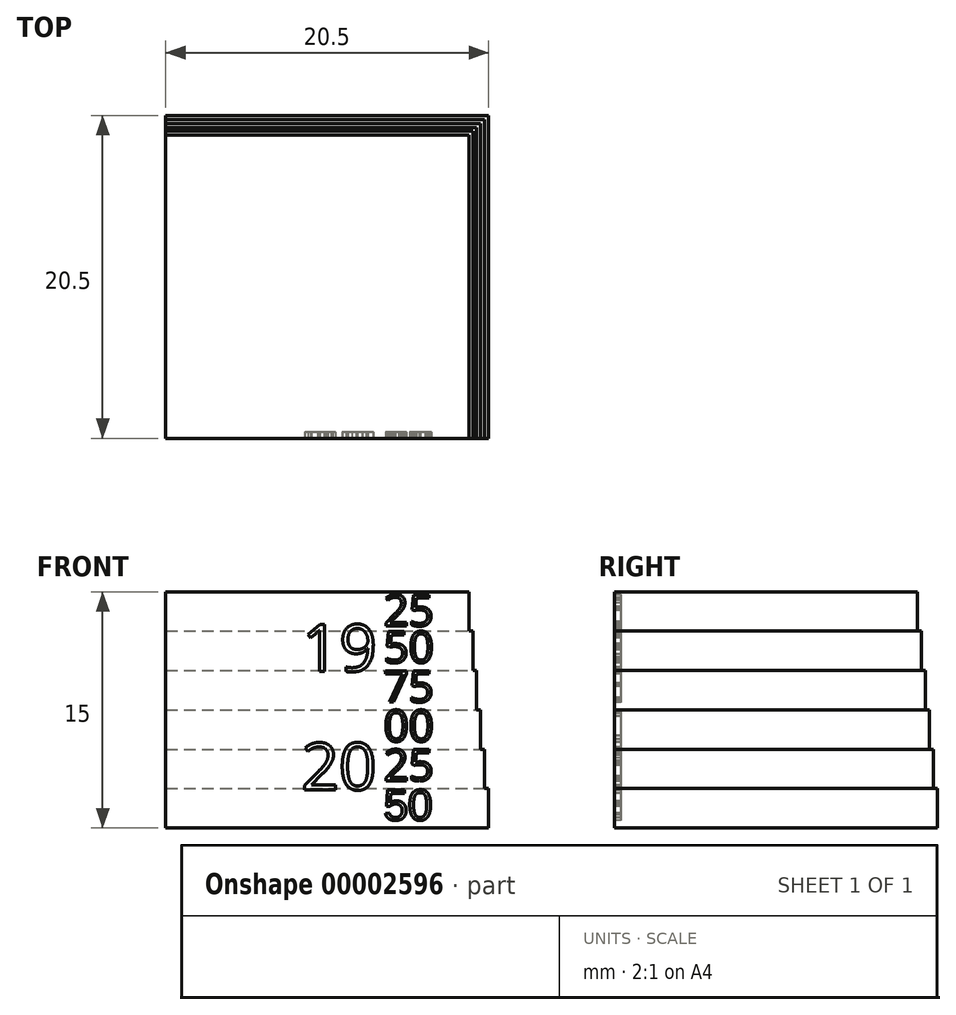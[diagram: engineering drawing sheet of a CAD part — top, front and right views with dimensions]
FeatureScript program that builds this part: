
annotation { "Feature Type Name" : "Feature", "Feature Type Description" : "" }
export const myFeature = defineFeature(function(context is Context, id is Id, definition is map)
    precondition{}
    {
        {
            var Q0;
            Q0=qCreatedBy(makeId("Top.planeOp"),FACE);
            var sketch = newSketch(context, id + "F0", { "sketchPlane" : qUnion([Q0])});
            skLineSegment(sketch, "E0.bottom", {"start": v(0, 0) * mm, "end": v(20.5, 0) * mm});
            skLineSegment(sketch, "E0.top", {"start": v(0, 20.5) * mm, "end": v(20.5, 20.5) * mm});
            skLineSegment(sketch, "E0.left", {"start": v(0, 0) * mm, "end": v(0, 20.5) * mm});
            skLineSegment(sketch, "E0.right", {"start": v(20.5, 0) * mm, "end": v(20.5, 20.5) * mm});
            skSolve(sketch);
        }
        {
            var Q0;
            Q0=makeQuery(id+"F0.imprint","IMPRINT",FACE,{"disambiguationData":[TD([[makeQuery(id+"F0.imprint","IMPRINT",EDGE,{"derivedFrom":sQuery(id+"F0.wireOp",EDGE,"E0.bottom")}),1.0]])]});
            extrude(context, id + "F1", {"entities" : qUnion([Q0]), "depth" : 2.5 * mm});
        }
        {
            var Q0;
            Q0=makeQuery(id+"F1.opExtrude","CAP_FACE",FACE,{"disambiguationData":[OSD([sQuery(id+"F0.wireOp",EDGE,"E0.bottom"),sQuery(id+"F0.wireOp",EDGE,"E0.top"),sQuery(id+"F0.wireOp",EDGE,"E0.left"),sQuery(id+"F0.wireOp",EDGE,"E0.right")])],"isStart":false});
            var sketch = newSketch(context, id + "F2", { "sketchPlane" : qUnion([Q0])});
            skLineSegment(sketch, "E1.bottom", {"start": v(0, 0) * mm, "end": v(20.25, 0) * mm});
            skLineSegment(sketch, "E1.top", {"start": v(0, 20.25) * mm, "end": v(20.25, 20.25) * mm});
            skLineSegment(sketch, "E1.left", {"start": v(0, 0) * mm, "end": v(0, 20.25) * mm});
            skLineSegment(sketch, "E1.right", {"start": v(20.25, 0) * mm, "end": v(20.25, 20.25) * mm});
            skSolve(sketch);
        }
        {
            var Q0;
            Q0 = qSketchRegion(id + "F2", true);
            extrude(context, id + "F3", {"entities" : qUnion([Q0]), "operationType" : NewBodyOperationType.ADD, "depth" : 2.5 * mm});
        }
        {
            var Q0;
            Q0=makeQuery(id+"F3.opExtrude","CAP_FACE",FACE,{"disambiguationData":[OSD([sQuery(id+"F2.wireOp",EDGE,"E1.bottom"),sQuery(id+"F2.wireOp",EDGE,"E1.top"),sQuery(id+"F2.wireOp",EDGE,"E1.left"),sQuery(id+"F2.wireOp",EDGE,"E1.right")])],"isStart":false});
            var sketch = newSketch(context, id + "F4", { "sketchPlane" : qUnion([Q0])});
            skLineSegment(sketch, "E2.bottom", {"start": v(0, 0) * mm, "end": v(20, 0) * mm});
            skLineSegment(sketch, "E2.top", {"start": v(0, 20) * mm, "end": v(20, 20) * mm});
            skLineSegment(sketch, "E2.left", {"start": v(0, 0) * mm, "end": v(0, 20) * mm});
            skLineSegment(sketch, "E2.right", {"start": v(20, 0) * mm, "end": v(20, 20) * mm});
            skSolve(sketch);
        }
        {
            var Q0;
            Q0 = qSketchRegion(id + "F4", true);
            extrude(context, id + "F5", {"entities" : qUnion([Q0]), "operationType" : NewBodyOperationType.ADD, "depth" : 2.5 * mm});
        }
        {
            var Q0;
            Q0=makeQuery(id+"F5.opExtrude","CAP_FACE",FACE,{"disambiguationData":[OSD([sQuery(id+"F4.wireOp",EDGE,"E2.bottom"),sQuery(id+"F4.wireOp",EDGE,"E2.top"),sQuery(id+"F4.wireOp",EDGE,"E2.left"),sQuery(id+"F4.wireOp",EDGE,"E2.right")])],"isStart":false});
            var sketch = newSketch(context, id + "F6", { "sketchPlane" : qUnion([Q0])});
            skLineSegment(sketch, "E3.bottom", {"start": v(0, 0) * mm, "end": v(19.75, 0) * mm});
            skLineSegment(sketch, "E3.top", {"start": v(0, 19.75) * mm, "end": v(19.75, 19.75) * mm});
            skLineSegment(sketch, "E3.left", {"start": v(0, 0) * mm, "end": v(0, 19.75) * mm});
            skLineSegment(sketch, "E3.right", {"start": v(19.75, 0) * mm, "end": v(19.75, 19.75) * mm});
            skSolve(sketch);
        }
        {
            var Q0;
            Q0=makeQuery(id+"F6.imprint","IMPRINT",FACE,{"disambiguationData":[TD([[makeQuery(id+"F6.imprint","IMPRINT",EDGE,{"derivedFrom":sQuery(id+"F6.wireOp",EDGE,"E3.bottom")}),1.0]])]});
            extrude(context, id + "F7", {"entities" : qUnion([Q0]), "operationType" : NewBodyOperationType.ADD, "depth" : 2.5 * mm});
        }
        {
            var Q0;
            Q0=makeQuery(id+"F7.opExtrude","CAP_FACE",FACE,{"disambiguationData":[OSD([sQuery(id+"F6.wireOp",EDGE,"E3.bottom"),sQuery(id+"F6.wireOp",EDGE,"E3.top"),sQuery(id+"F6.wireOp",EDGE,"E3.left"),sQuery(id+"F6.wireOp",EDGE,"E3.right")])],"isStart":false});
            var sketch = newSketch(context, id + "F8", { "sketchPlane" : qUnion([Q0])});
            skLineSegment(sketch, "E4.bottom", {"start": v(0, 0) * mm, "end": v(19.5, 0) * mm});
            skLineSegment(sketch, "E4.top", {"start": v(0, 19.5) * mm, "end": v(19.5, 19.5) * mm});
            skLineSegment(sketch, "E4.left", {"start": v(0, 0) * mm, "end": v(0, 19.5) * mm});
            skLineSegment(sketch, "E4.right", {"start": v(19.5, 0) * mm, "end": v(19.5, 19.5) * mm});
            skSolve(sketch);
        }
        {
            var Q0;
            Q0 = qSketchRegion(id + "F8", true);
            extrude(context, id + "F9", {"entities" : qUnion([Q0]), "operationType" : NewBodyOperationType.ADD, "depth" : 2.5 * mm});
        }
        {
            var Q0;
            Q0=makeQuery(id+"F9.opExtrude","CAP_FACE",FACE,{"disambiguationData":[OSD([sQuery(id+"F8.wireOp",EDGE,"E4.bottom"),sQuery(id+"F8.wireOp",EDGE,"E4.top"),sQuery(id+"F8.wireOp",EDGE,"E4.left"),sQuery(id+"F8.wireOp",EDGE,"E4.right")])],"isStart":false});
            var sketch = newSketch(context, id + "F10", { "sketchPlane" : qUnion([Q0])});
            skLineSegment(sketch, "E5.bottom", {"start": v(0, 0) * mm, "end": v(19.25, 0) * mm});
            skLineSegment(sketch, "E5.top", {"start": v(0, 19.25) * mm, "end": v(19.25, 19.25) * mm});
            skLineSegment(sketch, "E5.left", {"start": v(0, 0) * mm, "end": v(0, 19.25) * mm});
            skLineSegment(sketch, "E5.right", {"start": v(19.25, 0) * mm, "end": v(19.25, 19.25) * mm});
            skSolve(sketch);
        }
        {
            var Q0;
            Q0 = qSketchRegion(id + "F10", true);
            extrude(context, id + "F11", {"entities" : qUnion([Q0]), "operationType" : NewBodyOperationType.ADD, "depth" : 2.5 * mm});
        }
        {
            var Q0;
            Q0=makeQuery(id+"F11.boolean.opBoolean","MERGE",FACE,{"derivedFrom":[makeQuery(id+"F9.boolean.opBoolean","MERGE",FACE,{"derivedFrom":[makeQuery(id+"F7.boolean.opBoolean","MERGE",FACE,{"derivedFrom":[makeQuery(id+"F5.boolean.opBoolean","MERGE",FACE,{"derivedFrom":[makeQuery(id+"F3.boolean.opBoolean","MERGE",FACE,{"derivedFrom":[makeQuery(id+"F1.opExtrude","SWEPT_FACE",FACE,{"disambiguationData":[OSD([sQuery(id+"F0.wireOp",EDGE,"E0.bottom")])]}),makeQuery(id+"F3.opExtrude","SWEPT_FACE",FACE,{"disambiguationData":[OSD([sQuery(id+"F2.wireOp",EDGE,"E1.bottom")])]})]}),makeQuery(id+"F5.opExtrude","SWEPT_FACE",FACE,{"disambiguationData":[OSD([sQuery(id+"F4.wireOp",EDGE,"E2.bottom")])]})]}),makeQuery(id+"F7.opExtrude","SWEPT_FACE",FACE,{"disambiguationData":[OSD([sQuery(id+"F6.wireOp",EDGE,"E3.bottom")])]})]}),makeQuery(id+"F9.opExtrude","SWEPT_FACE",FACE,{"disambiguationData":[OSD([sQuery(id+"F8.wireOp",EDGE,"E4.bottom")])]})]}),makeQuery(id+"F11.opExtrude","SWEPT_FACE",FACE,{"disambiguationData":[OSD([sQuery(id+"F10.wireOp",EDGE,"E5.bottom")])]})]});
            var sketch = newSketch(context, id + "F12", { "sketchPlane" : qUnion([Q0])});
            skLineSegment(sketch, "E6.0", {"start": v(0, 15) * mm, "end": v(0, 0) * mm});
            skLineSegment(sketch, "E7.0", {"start": v(20.5, 2.5) * mm, "end": v(20.5, 0) * mm});
            skText(sketch, "E8", { "text": "50\n", "fontName": "Arimo-Regular.ttf"});
            skText(sketch, "E9", { "text": "25", "fontName": "OpenSans-Regular.ttf"});
            skText(sketch, "E10", { "text": "00", "fontName": "OpenSans-Regular.ttf"});
            skText(sketch, "E11", { "text": "75", "fontName": "OpenSans-Regular.ttf"});
            skText(sketch, "E12", { "text": "50\n", "fontName": "OpenSans-Regular.ttf"});
            skText(sketch, "E13", { "text": "25\n", "fontName": "OpenSans-Regular.ttf"});
            skLineSegment(sketch, "E14", {"start": v(13.84, 15) * mm, "end": v(13.84, 0) * mm, "construction": true});
            skText(sketch, "E15", { "text": "20\n", "fontName": "OpenSans-Regular.ttf"});
            skText(sketch, "E16", { "text": "19", "fontName": "OpenSans-Regular.ttf"});
            const initialGuessF12  = {"E8": [0.01384, 0.0005, 1, 0, 0.002], "E9": [0.01384, 0.003, 1, 0, 0.002], "E10": [0.01384, 0.0055, 1, 0, 0.002], "E11": [0.01384, 0.008, 1, 0, 0.002], "E12": [0.01384, 0.0105, 1, 0, 0.002], "E13": [0.01384, 0.01283, 1, 0, 0.002], "E15": [0.00862, 0.00242, 1, 0, 0.003], "E16": [0.00864, 0.00994, 1, 0, 0.003]};
            skSetInitialGuess(sketch, initialGuessF12);
            skSolve(sketch);
        }
        {
            var Q0;
            Q0 = qSketchRegion(id + "F12", true);
            extrude(context, id + "F13", {"entities" : qUnion([Q0]), "operationType" : NewBodyOperationType.REMOVE, "oppositeDirection" : true, "depth" : 0.4 * mm});
        }
    });
